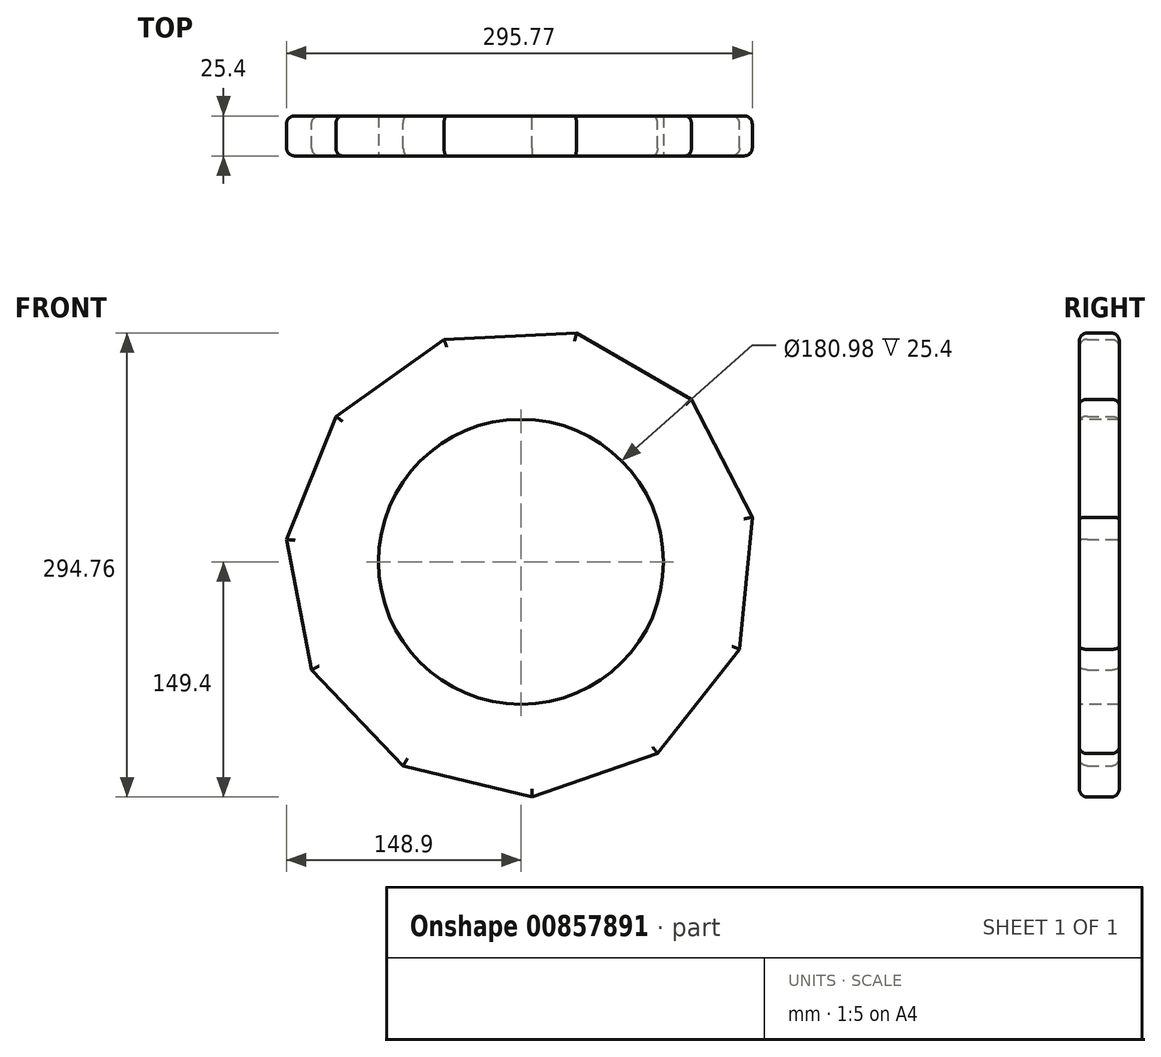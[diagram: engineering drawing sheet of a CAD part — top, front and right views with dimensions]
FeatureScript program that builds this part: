
annotation { "Feature Type Name" : "Feature", "Feature Type Description" : "" }
export const myFeature = defineFeature(function(context is Context, id is Id, definition is map)
    precondition{}
    {
        {
            var Q0;
            Q0=qCreatedBy(makeId("Front.planeOp"),FACE);
            var sketch = newSketch(context, id + "F0", { "sketchPlane" : qUnion([Q0])});
            skCircle(sketch, "E0.cCircle", {"center": v(0, 0) * mm, "radius": 71.76 * mm, "construction": true});
            skLineSegment(sketch, "E0.0", {"start": v(71.76, 124.29) * mm, "end": v(71.76, -124.29) * mm});
            skLineSegment(sketch, "E0.1", {"start": v(71.76, -124.29) * mm, "end": v(-143.51, 0) * mm});
            skLineSegment(sketch, "E0.2", {"start": v(-143.51, 0) * mm, "end": v(71.76, 124.29) * mm});
            skPoint(sketch, "E0.0.midPoint", {"position": v(71.76, 0) * mm});
            skCircle(sketch, "E1.cCircle", {"center": v(0, 3.5) * mm, "radius": 71.84 * mm, "construction": true});
            skLineSegment(sketch, "E1.0", {"start": v(72.9, 23.32) * mm, "end": v(70.62, -23.32) * mm});
            skLineSegment(sketch, "E1.1", {"start": v(70.62, -23.32) * mm, "end": v(41.37, -59.7) * mm});
            skLineSegment(sketch, "E1.2", {"start": v(41.37, -59.7) * mm, "end": v(-3.68, -71.95) * mm});
            skLineSegment(sketch, "E1.3", {"start": v(-3.68, -71.95) * mm, "end": v(-47.32, -55.38) * mm});
            skLineSegment(sketch, "E1.4", {"start": v(-47.32, -55.38) * mm, "end": v(-72.9, -16.32) * mm});
            skLineSegment(sketch, "E1.5", {"start": v(-72.9, -16.32) * mm, "end": v(-70.62, 30.3) * mm});
            skLineSegment(sketch, "E1.6", {"start": v(-70.62, 30.3) * mm, "end": v(-41.37, 66.7) * mm});
            skLineSegment(sketch, "E1.7", {"start": v(-41.37, 66.7) * mm, "end": v(3.68, 78.95) * mm});
            skLineSegment(sketch, "E1.8", {"start": v(3.68, 78.95) * mm, "end": v(47.32, 62.38) * mm});
            skLineSegment(sketch, "E1.9", {"start": v(47.32, 62.38) * mm, "end": v(72.9, 23.32) * mm});
            skLineSegment(sketch, "E2.0", {"start": v(35.26, 145.36) * mm, "end": v(108.25, 103.22) * mm});
            skLineSegment(sketch, "E2.1", {"start": v(108.25, 103.22) * mm, "end": v(146.87, 28.3) * mm});
            skLineSegment(sketch, "E2.2", {"start": v(146.87, 28.3) * mm, "end": v(138.86, -55.6) * mm});
            skLineSegment(sketch, "E2.3", {"start": v(138.86, -55.6) * mm, "end": v(86.76, -121.84) * mm});
            skLineSegment(sketch, "E2.4", {"start": v(86.76, -121.84) * mm, "end": v(7.12, -149.4) * mm});
            skLineSegment(sketch, "E2.5", {"start": v(7.12, -149.4) * mm, "end": v(-74.79, -129.53) * mm});
            skLineSegment(sketch, "E2.6", {"start": v(-74.79, -129.53) * mm, "end": v(-132.95, -68.54) * mm});
            skLineSegment(sketch, "E2.7", {"start": v(-132.95, -68.54) * mm, "end": v(-148.9, 14.22) * mm});
            skLineSegment(sketch, "E2.8", {"start": v(-148.9, 14.22) * mm, "end": v(-117.57, 92.46) * mm});
            skLineSegment(sketch, "E2.9", {"start": v(-117.57, 92.46) * mm, "end": v(-48.92, 141.35) * mm});
            skLineSegment(sketch, "E2.10", {"start": v(-48.92, 141.35) * mm, "end": v(35.26, 145.36) * mm});
            skPoint(sketch, "E2.0.midPoint", {"position": v(71.76, 124.29) * mm});
            skSolve(sketch);
        }
        {
            var Q0;
            {var subQ1=sQuery(id+"F0.wireOp",EDGE,"E0.1");Q0=makeQuery(id+"F0.imprint","IMPRINT",FACE,{"disambiguationData":[TD([[makeQuery(id+"F0.imprint","IMPRINT",EDGE,{"derivedFrom":subQ1}),-1.0]])]});}
            var Q1;
            {var subQ0=sQuery(id+"F0.wireOp",EDGE,"E1.8");Q1=makeQuery(id+"F0.imprint","IMPRINT",FACE,{"disambiguationData":[TD([[makeQuery(id+"F0.imprint","IMPRINT",EDGE,{"derivedFrom":subQ0}),1.0]])]});}
            var Q2;
            {var subQ0=sQuery(id+"F0.wireOp",EDGE,"E1.6");var subQ1=sQuery(id+"F0.wireOp",EDGE,"E0.2");var subQ2=makeQuery(id+"F0.imprint","INTERSECT",VERTEX,{"derivedFrom":[subQ1,subQ0]});Q2=makeQuery(id+"F0.imprint","IMPRINT",FACE,{"disambiguationData":[TD([[makeQuery(id+"F0.imprint","IMPRINT",EDGE,{"disambiguationData":[TD([[subQ2,-1.0]])],"derivedFrom":subQ1}),1.0]])]});}
            var Q3;
            {var subQ15=sQuery(id+"F0.wireOp",EDGE,"E0.1");Q3=makeQuery(id+"F0.imprint","IMPRINT",FACE,{"disambiguationData":[TD([[makeQuery(id+"F0.imprint","IMPRINT",EDGE,{"derivedFrom":subQ15}),1.0]])]});}
            extrude(context, id + "F1", {"entities" : qUnion([Q0, Q1, Q2, Q3]), "depth" : 25.4 * mm, "offsetDistance" : 25.4 * mm});
        }
        {
            var Q0;
            Q0=makeQuery(id+"F1.opExtrude","CAP_FACE",FACE,{"disambiguationData":[OSD([sQuery(id+"F0.wireOp",EDGE,"E0.2"),sQuery(id+"F0.wireOp",EDGE,"E1.0"),sQuery(id+"F0.wireOp",EDGE,"E1.1"),sQuery(id+"F0.wireOp",EDGE,"E1.2"),sQuery(id+"F0.wireOp",EDGE,"E1.3"),sQuery(id+"F0.wireOp",EDGE,"E1.4"),sQuery(id+"F0.wireOp",EDGE,"E1.5"),sQuery(id+"F0.wireOp",EDGE,"E1.6"),sQuery(id+"F0.wireOp",EDGE,"E1.7"),sQuery(id+"F0.wireOp",EDGE,"E1.8"),sQuery(id+"F0.wireOp",EDGE,"E1.9"),sQuery(id+"F0.wireOp",EDGE,"E2.0"),sQuery(id+"F0.wireOp",EDGE,"E2.1"),sQuery(id+"F0.wireOp",EDGE,"E2.2"),sQuery(id+"F0.wireOp",EDGE,"E2.3"),sQuery(id+"F0.wireOp",EDGE,"E2.4"),sQuery(id+"F0.wireOp",EDGE,"E2.5"),sQuery(id+"F0.wireOp",EDGE,"E2.6"),sQuery(id+"F0.wireOp",EDGE,"E2.7"),sQuery(id+"F0.wireOp",EDGE,"E2.8"),sQuery(id+"F0.wireOp",EDGE,"E2.9"),sQuery(id+"F0.wireOp",EDGE,"E2.10")])],"isStart":false});
            var sketch = newSketch(context, id + "F2", { "sketchPlane" : qUnion([Q0])});
            skCircle(sketch, "E3", {"center": v(0, 0) * mm, "radius": 90.5 * mm});
            skSolve(sketch);
        }
        {
            var Q0;
            Q0=makeQuery(id+"F2.imprint","IMPRINT",FACE,{"disambiguationData":[TD([[makeQuery(id+"F2.imprint","IMPRINT",EDGE,{"derivedFrom":sQuery(id+"F2.wireOp",EDGE,"E3")}),1.0]])]});
            extrude(context, id + "F3", {"entities" : qUnion([Q0]), "operationType" : NewBodyOperationType.REMOVE, "oppositeDirection" : true, "depth" : 25.4 * mm, "offsetDistance" : 25.4 * mm});
        }
        {
            var Q0;
            Q0=makeQuery(id+"F1.opExtrude","CAP_EDGE",EDGE,{"disambiguationData":[OSD([sQuery(id+"F0.wireOp",EDGE,"E2.8")])],"isStart":false});
            var Q1;
            Q1=makeQuery(id+"F1.opExtrude","CAP_EDGE",EDGE,{"disambiguationData":[OSD([sQuery(id+"F0.wireOp",EDGE,"E2.7")])],"isStart":false});
            var Q2;
            Q2=makeQuery(id+"F1.opExtrude","CAP_EDGE",EDGE,{"disambiguationData":[OSD([sQuery(id+"F0.wireOp",EDGE,"E2.6")])],"isStart":false});
            var Q3;
            Q3=makeQuery(id+"F1.opExtrude","CAP_EDGE",EDGE,{"disambiguationData":[OSD([sQuery(id+"F0.wireOp",EDGE,"E2.5")])],"isStart":false});
            var Q4;
            Q4=makeQuery(id+"F1.opExtrude","CAP_EDGE",EDGE,{"disambiguationData":[OSD([sQuery(id+"F0.wireOp",EDGE,"E2.4")])],"isStart":false});
            var Q5;
            Q5=makeQuery(id+"F1.opExtrude","CAP_EDGE",EDGE,{"disambiguationData":[OSD([sQuery(id+"F0.wireOp",EDGE,"E2.3")])],"isStart":false});
            var Q6;
            Q6=makeQuery(id+"F1.opExtrude","CAP_EDGE",EDGE,{"disambiguationData":[OSD([sQuery(id+"F0.wireOp",EDGE,"E2.2")])],"isStart":false});
            var Q7;
            Q7=makeQuery(id+"F1.opExtrude","CAP_EDGE",EDGE,{"disambiguationData":[OSD([sQuery(id+"F0.wireOp",EDGE,"E2.1")])],"isStart":false});
            var Q8;
            Q8=makeQuery(id+"F1.opExtrude","CAP_EDGE",EDGE,{"disambiguationData":[OSD([sQuery(id+"F0.wireOp",EDGE,"E2.0")])],"isStart":false});
            var Q9;
            Q9=makeQuery(id+"F1.opExtrude","CAP_EDGE",EDGE,{"disambiguationData":[OSD([sQuery(id+"F0.wireOp",EDGE,"E2.10")])],"isStart":false});
            var Q10;
            Q10=makeQuery(id+"F1.opExtrude","CAP_EDGE",EDGE,{"disambiguationData":[OSD([sQuery(id+"F0.wireOp",EDGE,"E2.9")])],"isStart":false});
            fillet(context, id + "F4", {"entities" : qUnion([Q0, Q1, Q2, Q3, Q4, Q5, Q6, Q7, Q8, Q9, Q10]), "radius" : 5.08 * mm, "tangentPropagation" : true, "allowEdgeOverflow" : false});
        }
        {
            var Q0;
            Q0=makeQuery(id+"F1.opExtrude","CAP_EDGE",EDGE,{"disambiguationData":[OSD([sQuery(id+"F0.wireOp",EDGE,"E2.1")])],"isStart":true});
            var Q1;
            Q1=makeQuery(id+"F1.opExtrude","CAP_EDGE",EDGE,{"disambiguationData":[OSD([sQuery(id+"F0.wireOp",EDGE,"E2.2")])],"isStart":true});
            var Q2;
            Q2=makeQuery(id+"F1.opExtrude","CAP_EDGE",EDGE,{"disambiguationData":[OSD([sQuery(id+"F0.wireOp",EDGE,"E2.3")])],"isStart":true});
            var Q3;
            Q3=makeQuery(id+"F1.opExtrude","CAP_EDGE",EDGE,{"disambiguationData":[OSD([sQuery(id+"F0.wireOp",EDGE,"E2.4")])],"isStart":true});
            var Q4;
            Q4=makeQuery(id+"F1.opExtrude","CAP_EDGE",EDGE,{"disambiguationData":[OSD([sQuery(id+"F0.wireOp",EDGE,"E2.5")])],"isStart":true});
            var Q5;
            Q5=makeQuery(id+"F1.opExtrude","CAP_EDGE",EDGE,{"disambiguationData":[OSD([sQuery(id+"F0.wireOp",EDGE,"E2.6")])],"isStart":true});
            var Q6;
            Q6=makeQuery(id+"F1.opExtrude","CAP_EDGE",EDGE,{"disambiguationData":[OSD([sQuery(id+"F0.wireOp",EDGE,"E2.7")])],"isStart":true});
            var Q7;
            Q7=makeQuery(id+"F1.opExtrude","CAP_EDGE",EDGE,{"disambiguationData":[OSD([sQuery(id+"F0.wireOp",EDGE,"E2.10")])],"isStart":true});
            var Q8;
            Q8=makeQuery(id+"F1.opExtrude","CAP_EDGE",EDGE,{"disambiguationData":[OSD([sQuery(id+"F0.wireOp",EDGE,"E2.0")])],"isStart":true});
            var Q9;
            Q9=makeQuery(id+"F1.opExtrude","CAP_EDGE",EDGE,{"disambiguationData":[OSD([sQuery(id+"F0.wireOp",EDGE,"E2.9")])],"isStart":true});
            var Q10;
            Q10=makeQuery(id+"F1.opExtrude","CAP_EDGE",EDGE,{"disambiguationData":[OSD([sQuery(id+"F0.wireOp",EDGE,"E2.8")])],"isStart":true});
            fillet(context, id + "F5", {"entities" : qUnion([Q0, Q1, Q2, Q3, Q4, Q5, Q6, Q7, Q8, Q9, Q10]), "radius" : 5.08 * mm, "tangentPropagation" : true, "allowEdgeOverflow" : false});
        }
    });
